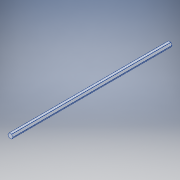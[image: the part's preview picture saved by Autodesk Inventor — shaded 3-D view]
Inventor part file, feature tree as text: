
AUTODESK INVENTOR PART (.ipt)
format: ipt  version: 2016 (Build 200138000, 138)  size: 139,776 bytes
history: native  units: in
note: dims shown in document units (in); Inventor stores cm internally (conversion verified against a paired STEP export)
features: extrude x1, sketch x1, projected_geometry x1, fillet x1
ambient origin geometry x8: Origin, YZ Plane, XZ Plane, XY Plane, X Axis, Y Axis, Z Axis, Center Point
bodies: Solid1 (feature_tree)
feature tree (4):
  extrude  "Extrusion1"  [1 undecoded]
  sketch  "Sketch1"  dims[d0=0.7542in d1=0.0in]
  projected_geometry  "Projected Loop1"
  fillet  "Fillet1"  [1 undecoded]
note: 2 required parameter values undecoded (feature->parameter linkage not recoverable at this tier; creation-order binding heuristic only, values carry confidence <= 0.55)
